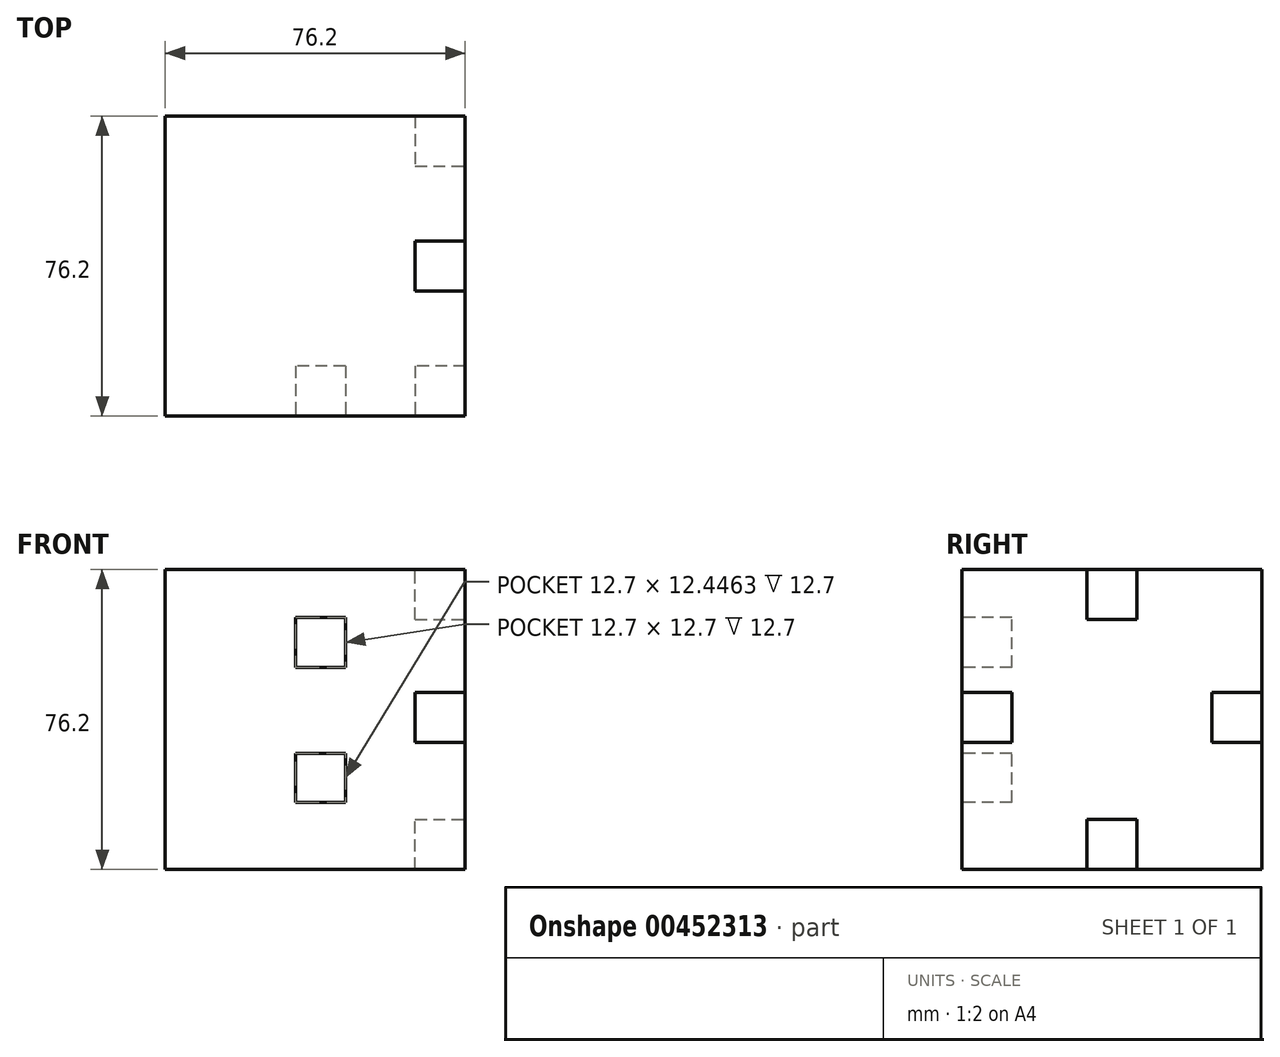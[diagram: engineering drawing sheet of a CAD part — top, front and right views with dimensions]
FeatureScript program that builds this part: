
annotation { "Feature Type Name" : "Feature", "Feature Type Description" : "" }
export const myFeature = defineFeature(function(context is Context, id is Id, definition is map)
    precondition{}
    {
        {
            var Q0;
            Q0=qCreatedBy(makeId("Front.planeOp"),FACE);
            var sketch = newSketch(context, id + "F0", { "sketchPlane" : qUnion([Q0])});
            skLineSegment(sketch, "E0.bottom", {"start": v(36.78, -38.67) * mm, "end": v(-39.42, -38.67) * mm});
            skLineSegment(sketch, "E0.top", {"start": v(36.78, 37.53) * mm, "end": v(-39.42, 37.53) * mm});
            skLineSegment(sketch, "E0.left", {"start": v(36.78, -38.67) * mm, "end": v(36.78, 37.53) * mm});
            skLineSegment(sketch, "E0.right", {"start": v(-39.42, -38.67) * mm, "end": v(-39.42, 37.53) * mm});
            skPoint(sketch, "E0.middle", {"position": v(-1.32, -0.57) * mm});
            skSolve(sketch);
        }
        {
            var Q0;
            Q0 = qSketchRegion(id + "F0", true);
            extrude(context, id + "F1", {"entities" : qUnion([Q0]), "depth" : 76.2 * mm});
        }
        {
            var Q0;
            Q0=makeQuery(id+"F1.opExtrude","CAP_FACE",FACE,{"disambiguationData":[OSD([sQuery(id+"F0.wireOp",EDGE,"E0.bottom"),sQuery(id+"F0.wireOp",EDGE,"E0.top"),sQuery(id+"F0.wireOp",EDGE,"E0.left"),sQuery(id+"F0.wireOp",EDGE,"E0.right")])],"isStart":false});
            var sketch = newSketch(context, id + "F2", { "sketchPlane" : qUnion([Q0])});
            skLineSegment(sketch, "E1.bottom", {"start": v(36.78, -6.35) * mm, "end": v(24.08, -6.35) * mm});
            skLineSegment(sketch, "E1.top", {"start": v(36.78, 6.35) * mm, "end": v(24.08, 6.35) * mm});
            skLineSegment(sketch, "E1.left", {"start": v(36.78, -6.35) * mm, "end": v(36.78, 6.35) * mm});
            skLineSegment(sketch, "E1.right", {"start": v(24.08, -6.35) * mm, "end": v(24.08, 6.35) * mm});
            skPoint(sketch, "E1.middle", {"position": v(30.43, 0) * mm});
            skSolve(sketch);
        }
        {
            var Q0;
            Q0 = qSketchRegion(id + "F2", true);
            extrude(context, id + "F3", {"entities" : qUnion([Q0]), "operationType" : NewBodyOperationType.REMOVE, "oppositeDirection" : true, "depth" : 12.7 * mm});
        }
        {
            var Q0;
            Q0=makeQuery(id+"F1.opExtrude","CAP_FACE",FACE,{"disambiguationData":[OSD([sQuery(id+"F0.wireOp",EDGE,"E0.bottom"),sQuery(id+"F0.wireOp",EDGE,"E0.top"),sQuery(id+"F0.wireOp",EDGE,"E0.left"),sQuery(id+"F0.wireOp",EDGE,"E0.right")])],"isStart":false});
            var sketch = newSketch(context, id + "F4", { "sketchPlane" : qUnion([Q0])});
            skPoint(sketch, "E2", {"position": v(0, 0) * mm});
            skPoint(sketch, "E3", {"position": v(0, 19.05) * mm});
            skLineSegment(sketch, "E4", {"start": v(0, 19.05) * mm, "end": v(0, 0) * mm});
            skLineSegment(sketch, "E5", {"start": v(0, 0) * mm, "end": v(0, -15.42) * mm});
            skLineSegment(sketch, "E6.bottom", {"start": v(6.35, 12.7) * mm, "end": v(-6.35, 12.7) * mm});
            skLineSegment(sketch, "E6.top", {"start": v(6.35, 25.4) * mm, "end": v(-6.35, 25.4) * mm});
            skLineSegment(sketch, "E6.left", {"start": v(6.35, 12.7) * mm, "end": v(6.35, 25.4) * mm});
            skLineSegment(sketch, "E6.right", {"start": v(-6.35, 12.7) * mm, "end": v(-6.35, 25.4) * mm});
            skLineSegment(sketch, "E7.bottom", {"start": v(6.35, -21.64) * mm, "end": v(-6.35, -21.64) * mm});
            skLineSegment(sketch, "E7.top", {"start": v(6.35, -9.2) * mm, "end": v(-6.35, -9.2) * mm});
            skLineSegment(sketch, "E7.left", {"start": v(6.35, -21.64) * mm, "end": v(6.35, -9.2) * mm});
            skLineSegment(sketch, "E7.right", {"start": v(-6.35, -21.64) * mm, "end": v(-6.35, -9.2) * mm});
            skPoint(sketch, "E7.middle", {"position": v(0, -15.42) * mm});
            skSolve(sketch);
        }
        {
            var Q0;
            Q0 = qSketchRegion(id + "F4", true);
            extrude(context, id + "F5", {"entities" : qUnion([Q0]), "operationType" : NewBodyOperationType.REMOVE, "oppositeDirection" : true, "depth" : 12.7 * mm});
        }
        {
            var Q0;
            Q0=makeQuery(id+"F1.opExtrude","SWEPT_FACE",FACE,{"disambiguationData":[OSD([sQuery(id+"F0.wireOp",EDGE,"E0.left")])]});
            var sketch = newSketch(context, id + "F6", { "sketchPlane" : qUnion([Q0])});
            skSolve(sketch);
        }
        {
            var Q0;
            {var subQ2=sQuery(id+"F0.wireOp",EDGE,"E0.left");Q0=makeQuery(id+"F6.imprint","IMPRINT",FACE,{"disambiguationData":[TD([[makeQuery(id+"F6.imprint","IMPRINT",EDGE,{"derivedFrom":makeQuery(id+"F1.opExtrude","CAP_EDGE",EDGE,{"disambiguationData":[OSD([subQ2])],"isStart":true})}),1.0]])]});}
            var sketch = newSketch(context, id + "F7", { "sketchPlane" : qUnion([Q0])});
            skLineSegment(sketch, "E8.bottom", {"start": v(0, -6.35) * mm, "end": v(-12.7, -6.35) * mm});
            skLineSegment(sketch, "E8.top", {"start": v(0, 6.35) * mm, "end": v(-12.7, 6.35) * mm});
            skLineSegment(sketch, "E8.left", {"start": v(0, -6.35) * mm, "end": v(0, 6.35) * mm});
            skLineSegment(sketch, "E8.right", {"start": v(-12.7, -6.35) * mm, "end": v(-12.7, 6.35) * mm});
            skPoint(sketch, "E8.middle", {"position": v(-6.35, 0) * mm});
            skPoint(sketch, "E9", {"position": v(-38.07, 0) * mm});
            skPoint(sketch, "E10", {"position": v(-38.07, -32.36) * mm});
            skPoint(sketch, "E11", {"position": v(-38.07, -38.71) * mm});
            skPoint(sketch, "E12", {"position": v(-31.75, -38.71) * mm});
            skLineSegment(sketch, "E13.bottom", {"start": v(-31.75, -38.71) * mm, "end": v(-44.4, -38.71) * mm});
            skLineSegment(sketch, "E13.top", {"start": v(-31.75, -26.01) * mm, "end": v(-44.4, -26.01) * mm});
            skLineSegment(sketch, "E13.left", {"start": v(-31.75, -38.71) * mm, "end": v(-31.75, -26.01) * mm});
            skLineSegment(sketch, "E13.right", {"start": v(-44.4, -38.71) * mm, "end": v(-44.4, -26.01) * mm});
            skPoint(sketch, "E14", {"position": v(-38.07, 37.53) * mm});
            skPoint(sketch, "E15", {"position": v(-38.07, 31.18) * mm});
            skLineSegment(sketch, "E16.bottom", {"start": v(-31.72, 24.83) * mm, "end": v(-44.42, 24.83) * mm});
            skLineSegment(sketch, "E16.top", {"start": v(-31.72, 37.53) * mm, "end": v(-44.42, 37.53) * mm});
            skLineSegment(sketch, "E16.left", {"start": v(-31.72, 24.83) * mm, "end": v(-31.72, 37.53) * mm});
            skLineSegment(sketch, "E16.right", {"start": v(-44.42, 24.83) * mm, "end": v(-44.42, 37.53) * mm});
            skSolve(sketch);
        }
        {
            var Q0;
            Q0 = qSketchRegion(id + "F7", true);
            extrude(context, id + "F8", {"entities" : qUnion([Q0]), "operationType" : NewBodyOperationType.REMOVE, "oppositeDirection" : true, "depth" : 12.7 * mm});
        }
    });
